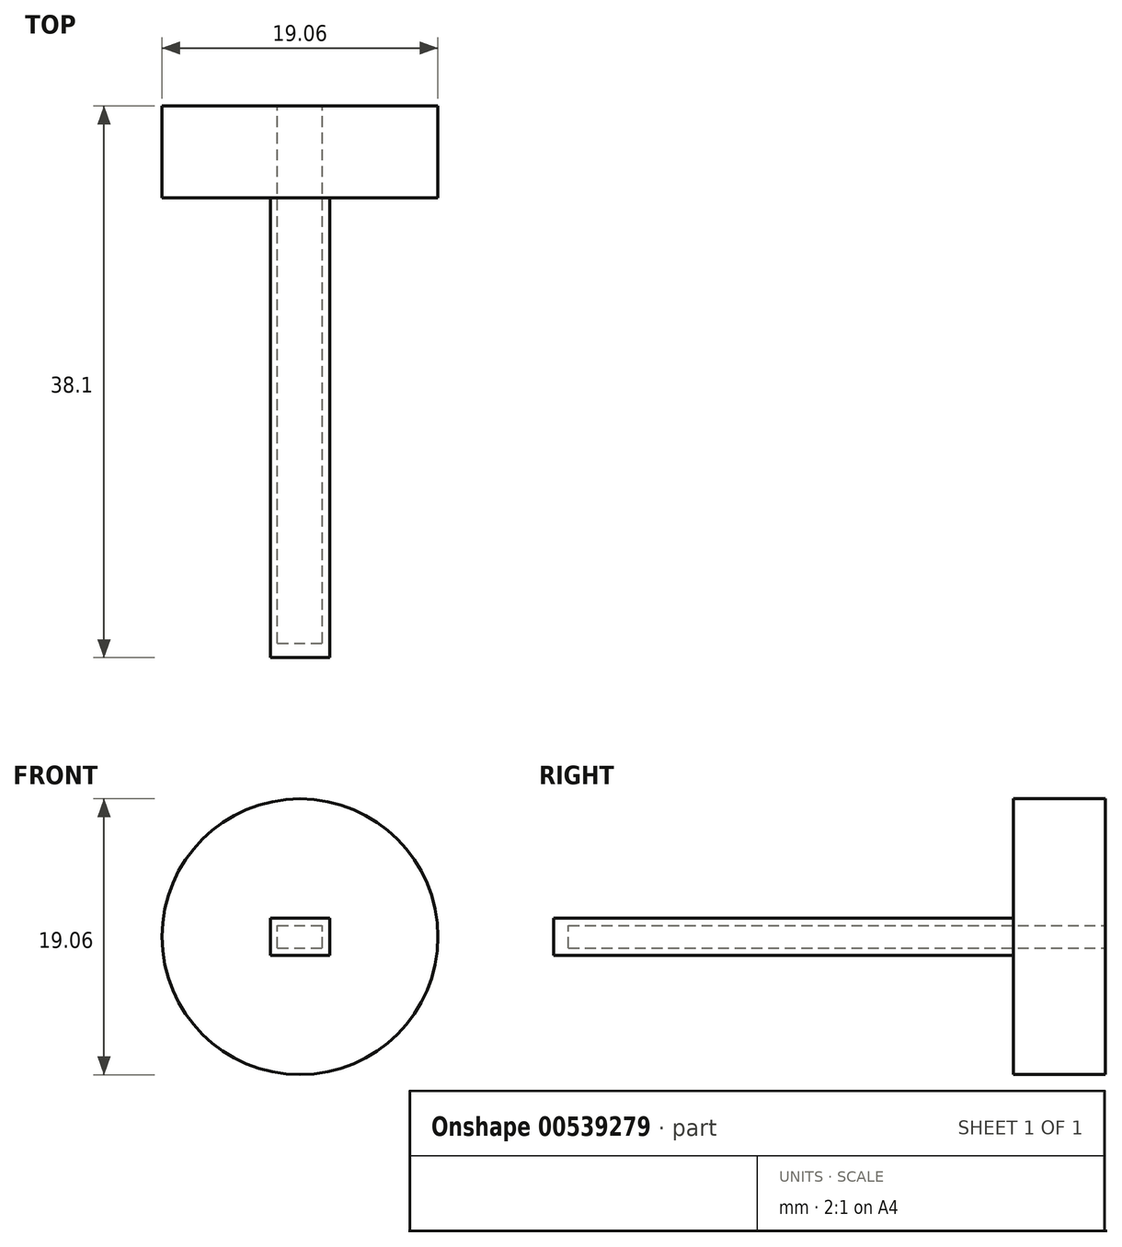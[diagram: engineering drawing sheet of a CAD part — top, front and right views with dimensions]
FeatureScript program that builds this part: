
annotation { "Feature Type Name" : "Feature", "Feature Type Description" : "" }
export const myFeature = defineFeature(function(context is Context, id is Id, definition is map)
    precondition{}
    {
        {
            var Q0;
            Q0=qCreatedBy(makeId("Front.planeOp"),FACE);
            var sketch = newSketch(context, id + "F0", { "sketchPlane" : qUnion([Q0])});
            skLineSegment(sketch, "E0.bottom", {"start": v(-1.55, -0.78) * mm, "end": v(1.55, -0.78) * mm});
            skLineSegment(sketch, "E0.top", {"start": v(-1.55, 0.77) * mm, "end": v(1.55, 0.77) * mm});
            skLineSegment(sketch, "E0.left", {"start": v(-1.55, -0.78) * mm, "end": v(-1.55, 0.77) * mm});
            skLineSegment(sketch, "E0.right", {"start": v(1.55, -0.78) * mm, "end": v(1.55, 0.77) * mm});
            skPoint(sketch, "E0.middle", {"position": v(0, 0) * mm});
            skLineSegment(sketch, "E1.bottom", {"start": v(2.05, 1.28) * mm, "end": v(-2.05, 1.27) * mm});
            skLineSegment(sketch, "E1.top", {"start": v(2.05, -1.27) * mm, "end": v(-2.05, -1.28) * mm});
            skLineSegment(sketch, "E1.left", {"start": v(2.05, 1.28) * mm, "end": v(2.05, -1.27) * mm});
            skLineSegment(sketch, "E1.right", {"start": v(-2.05, 1.27) * mm, "end": v(-2.05, -1.28) * mm});
            skCircle(sketch, "E2", {"center": v(0, 0) * mm, "radius": 9.53 * mm});
            skSolve(sketch);
        }
        {
            var Q0;
            Q0=makeQuery(id+"F0.imprint","IMPRINT",FACE,{"disambiguationData":[TD([[makeQuery(id+"F0.imprint","IMPRINT",EDGE,{"derivedFrom":sQuery(id+"F0.wireOp",EDGE,"E0.bottom")}),-1.0]])]});
            extrude(context, id + "F1", {"entities" : qUnion([Q0]), "depth" : 38.1 * mm, "offsetDistance" : 25 * mm});
        }
        {
            var Q0;
            Q0=makeQuery(id+"F0.imprint","IMPRINT",FACE,{"disambiguationData":[TD([[makeQuery(id+"F0.imprint","IMPRINT",EDGE,{"derivedFrom":sQuery(id+"F0.wireOp",EDGE,"E1.bottom")}),-1.0]])]});
            extrude(context, id + "F2", {"entities" : qUnion([Q0]), "operationType" : NewBodyOperationType.ADD, "depth" : 6.35 * mm, "offsetDistance" : 25 * mm});
        }
        {
            var Q0;
            Q0=makeQuery(id+"F1.opExtrude","CAP_FACE",FACE,{"disambiguationData":[OSD([sQuery(id+"F0.wireOp",EDGE,"E0.bottom"),sQuery(id+"F0.wireOp",EDGE,"E0.top"),sQuery(id+"F0.wireOp",EDGE,"E0.left"),sQuery(id+"F0.wireOp",EDGE,"E0.right"),sQuery(id+"F0.wireOp",EDGE,"E1.bottom"),sQuery(id+"F0.wireOp",EDGE,"E1.top"),sQuery(id+"F0.wireOp",EDGE,"E1.left"),sQuery(id+"F0.wireOp",EDGE,"E1.right")])],"isStart":false});
            var sketch = newSketch(context, id + "F3", { "sketchPlane" : qUnion([Q0])});
            skLineSegment(sketch, "E3.bottom", {"start": v(-2.05, -1.28) * mm, "end": v(2.05, -1.28) * mm});
            skLineSegment(sketch, "E3.top", {"start": v(-2.05, 1.28) * mm, "end": v(2.05, 1.28) * mm});
            skLineSegment(sketch, "E3.left", {"start": v(-2.05, -1.28) * mm, "end": v(-2.05, 1.28) * mm});
            skLineSegment(sketch, "E3.right", {"start": v(2.05, -1.28) * mm, "end": v(2.05, 1.28) * mm});
            skPoint(sketch, "E3.middle", {"position": v(0, 0) * mm});
            skSolve(sketch);
        }
        {
            var Q0;
            Q0=makeQuery(id+"F3.imprint","IMPRINT",FACE,{"disambiguationData":[TD([[makeQuery(id+"F3.imprint","IMPRINT",EDGE,{"derivedFrom":sQuery(id+"F3.wireOp",EDGE,"E3.bottom")}),-1.0]])]});
            var Q1;
            Q1=makeQuery(id+"F3.imprint","IMPRINT",FACE,{"disambiguationData":[TD([[makeQuery(id+"F3.imprint","IMPRINT",EDGE,{"derivedFrom":makeQuery(id+"F1.opExtrude","CAP_EDGE",EDGE,{"disambiguationData":[OSD([sQuery(id+"F0.wireOp",EDGE,"E0.bottom")])],"isStart":false})}),1.0]])]});
            extrude(context, id + "F4", {"entities" : qUnion([Q0, Q1]), "operationType" : NewBodyOperationType.ADD, "oppositeDirection" : true, "depth" : 1 * mm, "offsetDistance" : 25 * mm});
        }
    });
